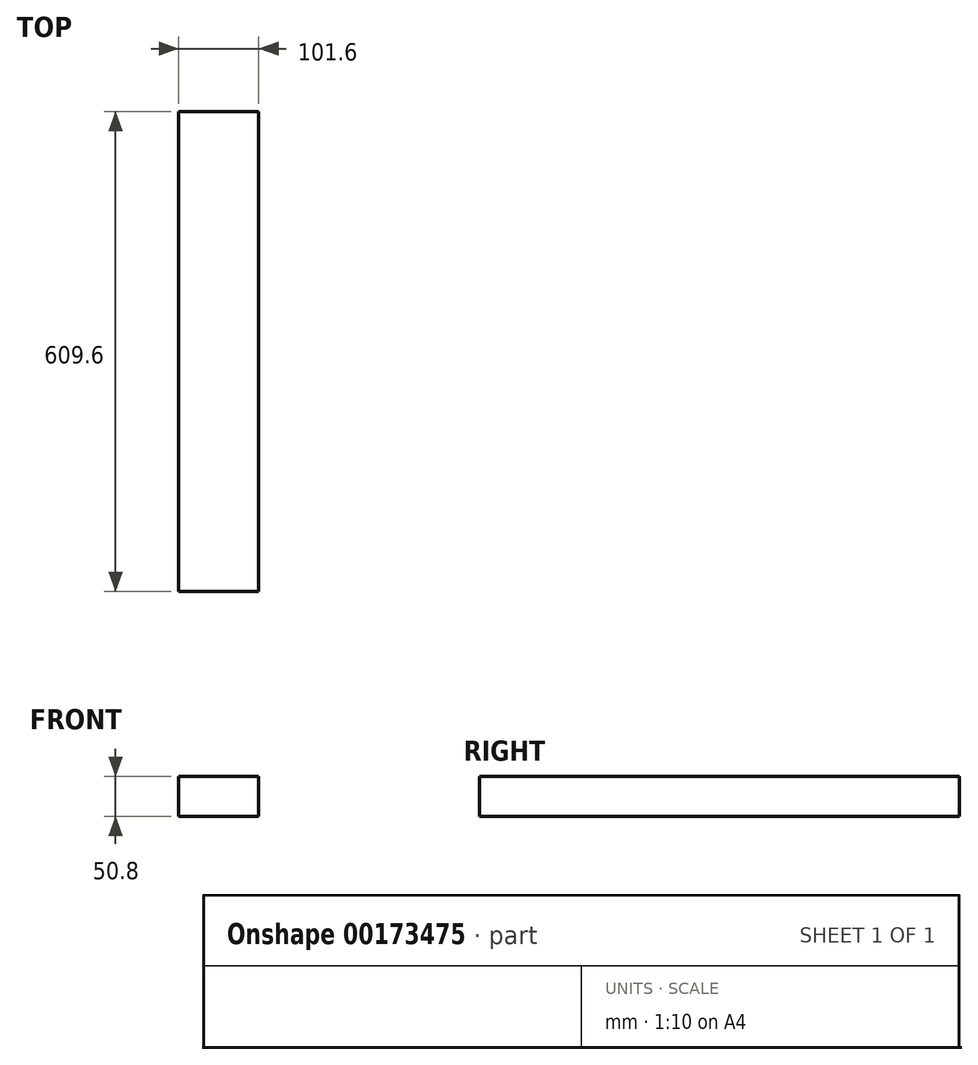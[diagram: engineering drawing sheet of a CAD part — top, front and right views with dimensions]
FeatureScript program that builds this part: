
annotation { "Feature Type Name" : "Feature", "Feature Type Description" : "" }
export const myFeature = defineFeature(function(context is Context, id is Id, definition is map)
    precondition{}
    {
        {
            var Q0;
            Q0=qCreatedBy(makeId("Front.planeOp"),FACE);
            var sketch = newSketch(context, id + "F0", { "sketchPlane" : qUnion([Q0])});
            skLineSegment(sketch, "E0.bottom", {"start": v(50.8, 25.4) * mm, "end": v(-50.8, 25.4) * mm});
            skLineSegment(sketch, "E0.top", {"start": v(50.8, -25.4) * mm, "end": v(-50.8, -25.4) * mm});
            skLineSegment(sketch, "E0.left", {"start": v(50.8, 25.4) * mm, "end": v(50.8, -25.4) * mm});
            skLineSegment(sketch, "E0.right", {"start": v(-50.8, 25.4) * mm, "end": v(-50.8, -25.4) * mm});
            skPoint(sketch, "E0.middle", {"position": v(0, 0) * mm});
            skSolve(sketch);
        }
        {
            var Q0;
            Q0 = qSketchRegion(id + "F0", true);
            extrude(context, id + "F1", {"entities" : qUnion([Q0]), "depth" : 609.6 * mm});
        }
    });
